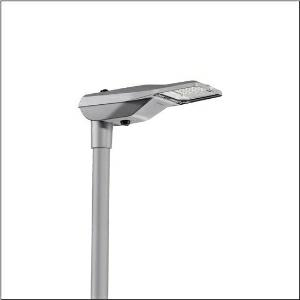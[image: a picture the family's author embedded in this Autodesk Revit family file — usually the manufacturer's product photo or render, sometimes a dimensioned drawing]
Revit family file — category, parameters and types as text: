
# Revit family: streetlight_sl_21_micro___stw1_0a_5xe1e33t08db_9129
name_source: partatom
category: Lighting Fixtures
units: mm (PartAtom-declared; Revit-internal decimal feet)

## family parameters
Cut with Voids When Loaded = No
Host = Face
Light Source = No
Part Type = Normal
Room Calculation Point = No
Round Connector Dimension = Use Diameter
Shared = No

## types (1)
- --- (1 x LED, 5110 lm, 39.1 W, 3000K)
    Apparent Load = 39 VA
    CIE Flux Codes = 38 75 98 100 100
    Color Rendering = 70
    Color Temperature = 3000K
    Default Elevation = 1800 mm
    Description = Streetlight SL 21 micro, mast luminaire, primary light control with lens, of PMMA, primary optical cover: cover, of toughened safety glass, transparent, light distribution: STW1.0a, light emission: direct distribution, primary light characteristic: asymmetric, installation type: side-entry, post-top, LED, High Power LED, rated luminous flux: 5.110lm, luminous efficacy: 131lm/W, light colour: 730, colour temperature: 3000K, control gear: D4i, control: flexible luminous flux parameterisation, time-dependent luminous flux control, constant luminous flux control, overheat protection, pre-setting: logarithmic dimming characteristic, mains connection: 220..240V, AC, 50/60Hz, start of lifetime: 39W, end of service life: 41W, reduction: 18W, luminaire housing, of diecast aluminium, powder-coated, SITECO metallic grey (DB 702S), corrosivity category C5 high according to DIN EN ISO 12944, please order mast flange separately, inclination adjustable: 0°, 5°, 10°, 15°, sealing non-destructively replaceable, multi-level sealing system, length: 528mm, width: 235mm, height: 110mm, mast flange for spigot size: 42mm (side-entry): 5XC10008XM4, 60/48mm (side-entry/post-top): 5XC10108XM2, 76/60mm (side-entry/post-top): 5XC10108XM1, Smart Interface below and above, protection rating (complete): IP66, insulation class (complete): insulation class II (safety insulation), certification: CE, ENEC, ENEC+, VDE, impact resistance: IK10, permissible operating ambient temperature for outdoor applications: -40..+50°C, standard-compliant lighting for roads and squares, packaging unit: 1 piece

Light Distribution: STW1.0a
    Height = 110 mm
    Lamp = 1 x LED
    Lamp Light Flux = 5110 lm
    Lamp Power = 39.1 W
    Lamp count = 1
    Length = 528 mm
    Luminous efficacy = 131 lm/W
    Manufacturer = Siteco
    ModVariant = No
    Model = 5XE1E33T08DB
    Number of Poles = 1
    OnlyDefault = Yes
    Power Factor = 1
    Product Name = Streetlight SL 21 micro | STW1.0a
    Product group = mast luminaire | pylon top
    ProductGroupID = 6100
    Protection Class = Protection class II
    Protection Degree = IP 66
    RLX_Detail_Level = 1
    RLX_Emergency_Light_Flux = 0 lm
    RLX_Emergency_Type = 0
    RLX_Emergency_Type_DB = No
    RlxData = <blob elided: 98121 chars, md5=fc714695>
    Socket = socket
    Standby Power = 0 W
    System Light Flux = 5110 lm
    System Power = 39 W
    Type Comments = factory setting: luminous flux: 100 % | dim-lin: 254 | 765 mA
    Type Image = l_1007239.jpg
    URL = http://relux.com
    VarID = @adj_154763
    Voltage = 0 V
    Weight = 0.00 kg
    Width = 235 mm

## geometry (parser evidence)
native form markers: Blend x4, Sweep x9
no freeform markers — native parametric forms only
